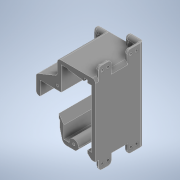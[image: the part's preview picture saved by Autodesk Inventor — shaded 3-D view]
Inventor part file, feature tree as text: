
AUTODESK INVENTOR PART (.ipt)
format: ipt  version: 2022 (Build 260153000, 153)  size: 1,026,048 bytes
history: native  units: mm
features: extrude x9, sketch x5, projected_geometry x4, fillet x3, other x2, chamfer x1
ambient origin geometry x8: Origin, YZ Plane, XZ Plane, XY Plane, X Axis, Y Axis, Z Axis, Center Point
bodies: Body1 (feature_tree)
feature tree (24):
  other  "Твердое тело1"
  extrude  "Выдавливание1"  Depth=40.0mm
  sketch  "Эскиз2"
  extrude  "Выдавливание2"  Depth=50.0mm
  extrude  "Выдавливание3"  Depth=1.0mm TaperAngle=0.0deg
  extrude  "Выдавливание4"  Depth=4.2mm
  extrude  "Выдавливание6"  Depth=2.2mm
  chamfer  "Фаска1"  Distance=1.7mm
  extrude  "Выдавливание7"  Depth=40.4mm
  extrude  "Выдавливание8"  Depth=1.7mm
  fillet  "Сопряжение1"  Radius=2.5mm
  extrude  "Выдавливание9"  Depth=15.0mm
  fillet  "Сопряжение2"  Radius=2.5mm
  other  "РабПлоскость3"
  extrude  "Выдавливание10"  Depth=2.5mm
  fillet  "Сопряжение3"  Radius=2.5mm
  sketch  "Эскиз1"
  sketch  "Эскиз3"
  projected_geometry  "Спроецированная петля1"
  sketch  "Эскиз4"
  projected_geometry  "Спроецированная петля2"
  projected_geometry  "Спроецированная петля3"
  projected_geometry  "Спроецированная петля4"
  sketch  "Эскиз6"
